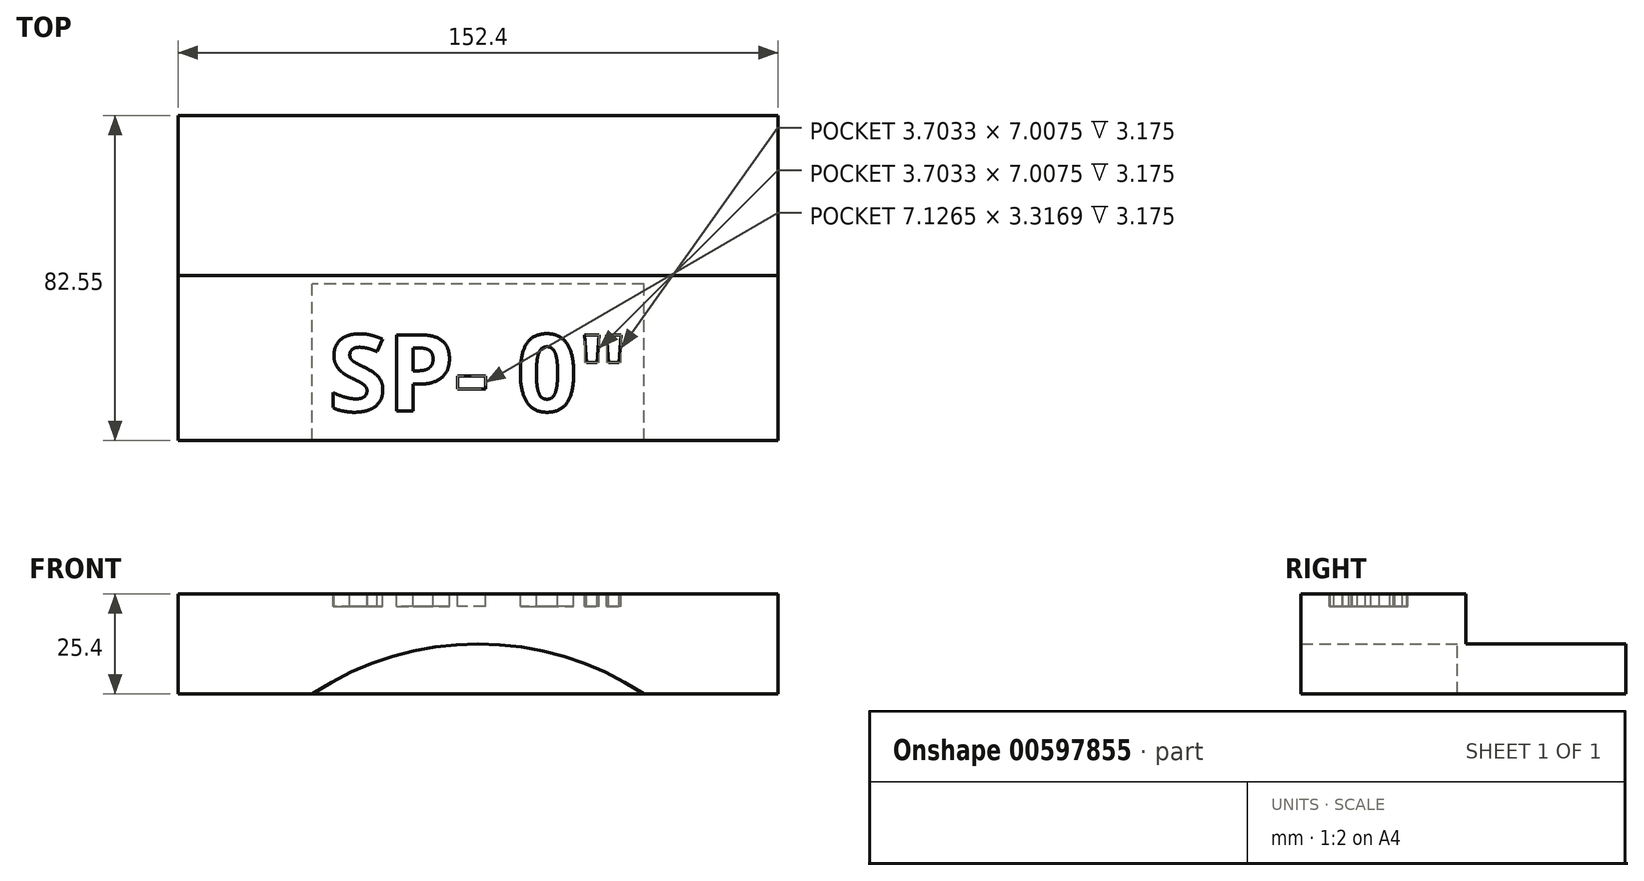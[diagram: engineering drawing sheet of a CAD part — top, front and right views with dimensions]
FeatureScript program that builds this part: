
annotation { "Feature Type Name" : "Feature", "Feature Type Description" : "" }
export const myFeature = defineFeature(function(context is Context, id is Id, definition is map)
    precondition{}
    {
        {
            var Q0;
            Q0=qCreatedBy(makeId("Front.planeOp"),FACE);
            var sketch = newSketch(context, id + "F0", { "sketchPlane" : qUnion([Q0])});
            skLineSegment(sketch, "E0.bottom", {"start": v(0, 0) * mm, "end": v(34.08, 0) * mm});
            skLineSegment(sketch, "E0.top", {"start": v(0, 25.4) * mm, "end": v(152.4, 25.4) * mm});
            skLineSegment(sketch, "E0.left", {"start": v(0, 0) * mm, "end": v(0, 25.4) * mm});
            skLineSegment(sketch, "E0.right", {"start": v(152.4, 0) * mm, "end": v(152.4, 25.4) * mm});
            skArc(sketch, "E1", {"start": v(118.32, 0) * mm, "mid": v(76.2, 12.7) * mm, "end": v(34.08, 0) * mm});
            skPoint(sketch, "E1.centerSnap0", {"position": v(76.2, 0) * mm});
            skLineSegment(sketch, "E2.trimOffspring", {"start": v(118.32, 0) * mm, "end": v(152.4, 0) * mm});
            skLineSegment(sketch, "E3", {"start": v(152.4, 12.7) * mm, "end": v(0, 12.7) * mm, "construction": true});
            skSolve(sketch);
        }
        {
            var Q0;
            Q0 = qSketchRegion(id + "F0", true);
            extrude(context, id + "F1", {"entities" : qUnion([Q0]), "depth" : 39.69 * mm, "offsetDistance" : 25.4 * mm});
        }
        {
            var Q0;
            Q0=makeQuery(id+"F1.opExtrude","CAP_FACE",FACE,{"disambiguationData":[OSD([sQuery(id+"F0.wireOp",EDGE,"E0.bottom"),sQuery(id+"F0.wireOp",EDGE,"E0.top"),sQuery(id+"F0.wireOp",EDGE,"E0.left"),sQuery(id+"F0.wireOp",EDGE,"E0.right"),sQuery(id+"F0.wireOp",EDGE,"E1"),sQuery(id+"F0.wireOp",EDGE,"E2.trimOffspring")])],"isStart":true});
            var sketch = newSketch(context, id + "F2", { "sketchPlane" : qUnion([Q0])});
            skLineSegment(sketch, "E4.bottom", {"start": v(-152.4, 0) * mm, "end": v(0, 0) * mm});
            skLineSegment(sketch, "E4.top", {"start": v(-152.4, 25.4) * mm, "end": v(0, 25.4) * mm});
            skLineSegment(sketch, "E4.left", {"start": v(-152.4, 0) * mm, "end": v(-152.4, 25.4) * mm});
            skLineSegment(sketch, "E4.right", {"start": v(0, 0) * mm, "end": v(0, 25.4) * mm});
            skSolve(sketch);
        }
        {
            var Q0;
            Q0 = qSketchRegion(id + "F2", true);
            extrude(context, id + "F3", {"entities" : qUnion([Q0]), "operationType" : NewBodyOperationType.ADD, "depth" : 42.86 * mm, "offsetDistance" : 25.4 * mm});
        }
        {
            var Q0;
            Q0=makeQuery(id+"F3.opExtrude","CAP_FACE",FACE,{"disambiguationData":[OSD([sQuery(id+"F2.wireOp",EDGE,"E4.bottom"),sQuery(id+"F2.wireOp",EDGE,"E4.top"),sQuery(id+"F2.wireOp",EDGE,"E4.left"),sQuery(id+"F2.wireOp",EDGE,"E4.right")])],"isStart":false});
            var sketch = newSketch(context, id + "F4", { "sketchPlane" : qUnion([Q0])});
            skLineSegment(sketch, "E5.bottom", {"start": v(0, 25.4) * mm, "end": v(-152.4, 25.4) * mm});
            skLineSegment(sketch, "E5.top", {"start": v(0, 12.7) * mm, "end": v(-152.4, 12.7) * mm});
            skLineSegment(sketch, "E5.left", {"start": v(0, 25.4) * mm, "end": v(0, 12.7) * mm});
            skLineSegment(sketch, "E5.right", {"start": v(-152.4, 25.4) * mm, "end": v(-152.4, 12.7) * mm});
            skSolve(sketch);
        }
        {
            var Q0;
            Q0 = qSketchRegion(id + "F4", true);
            extrude(context, id + "F5", {"entities" : qUnion([Q0]), "operationType" : NewBodyOperationType.REMOVE, "oppositeDirection" : true, "depth" : 40.64 * mm, "offsetDistance" : 25.4 * mm});
        }
        {
            var Q0;
            Q0=makeQuery(id+"F3.boolean.opBoolean","MERGE",FACE,{"derivedFrom":[makeQuery(id+"F1.opExtrude","SWEPT_FACE",FACE,{"disambiguationData":[OSD([sQuery(id+"F0.wireOp",EDGE,"E0.top")])]}),makeQuery(id+"F3.opExtrude","SWEPT_FACE",FACE,{"disambiguationData":[OSD([sQuery(id+"F2.wireOp",EDGE,"E4.top")])]})]});
            var sketch = newSketch(context, id + "F6", { "sketchPlane" : qUnion([Q0])});
            skText(sketch, "E6", { "text": "SP- 0\"", "fontName": "OpenSans-Bold.ttf"});
            const initialGuessF6  = {"E6": [0.0381, -0.03226, 1, 0, 0.01957]};
            skSetInitialGuess(sketch, initialGuessF6);
            skSolve(sketch);
        }
        {
            var Q0;
            Q0 = qSketchRegion(id + "F6", true);
            extrude(context, id + "F7", {"entities" : qUnion([Q0]), "operationType" : NewBodyOperationType.REMOVE, "oppositeDirection" : true, "depth" : 3.17 * mm, "offsetDistance" : 25.4 * mm});
        }
    });
